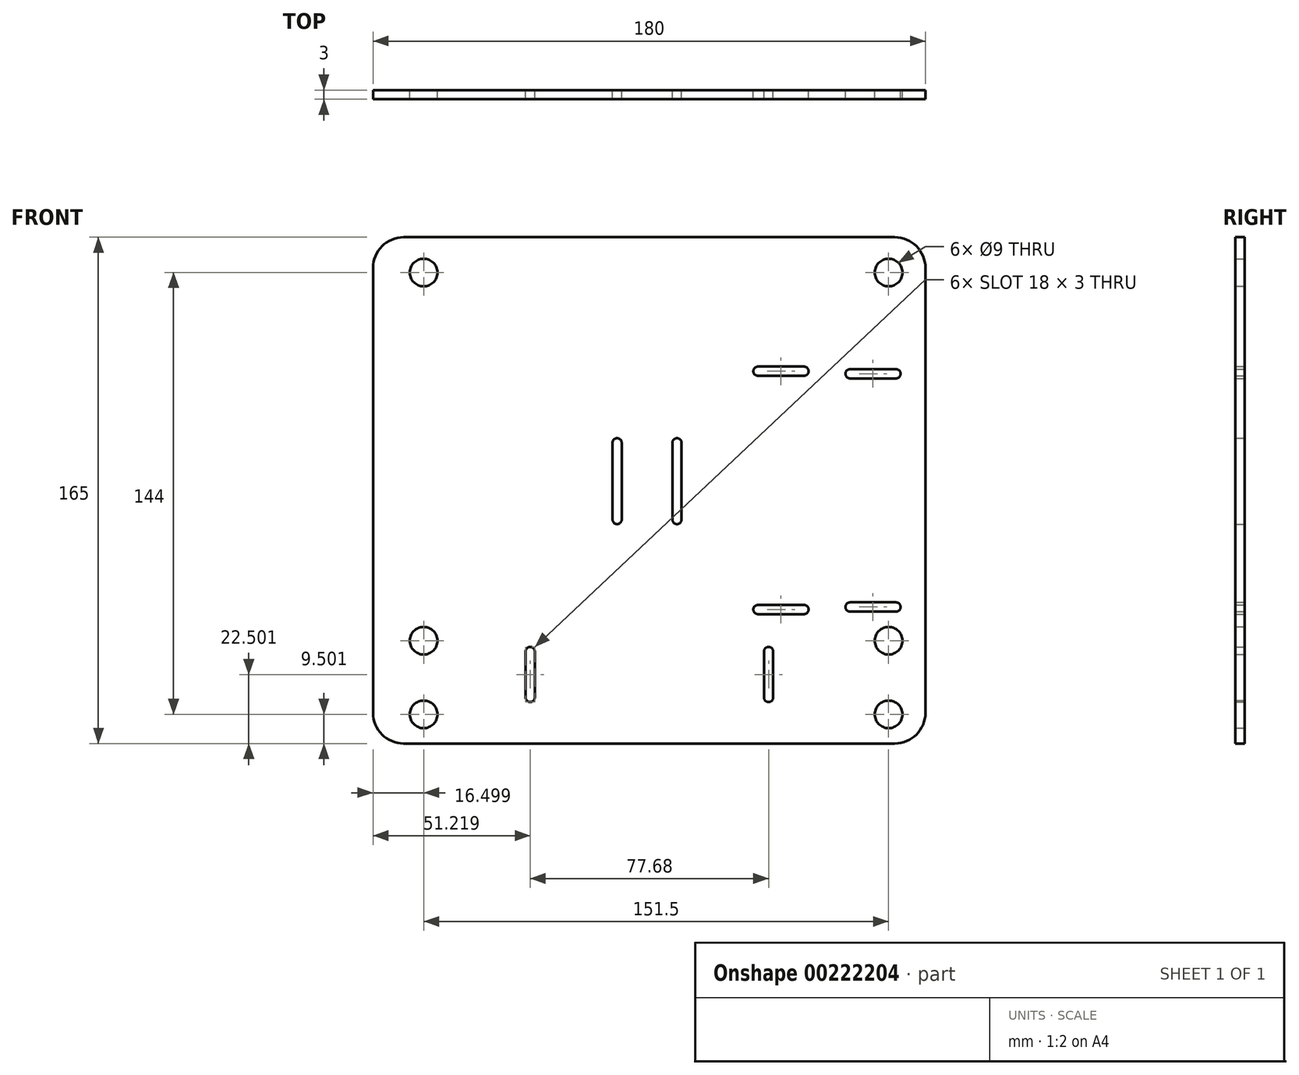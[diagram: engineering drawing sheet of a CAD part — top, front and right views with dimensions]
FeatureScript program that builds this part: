
annotation { "Feature Type Name" : "Feature", "Feature Type Description" : "" }
export const myFeature = defineFeature(function(context is Context, id is Id, definition is map)
    precondition{}
    {
        {
            var Q0;
            Q0=qCreatedBy(makeId("Front.planeOp"),FACE);
            var sketch = newSketch(context, id + "F0", { "sketchPlane" : qUnion([Q0])});
            skLineSegment(sketch, "E0", {"start": v(-133.42, 78.54) * mm, "end": v(-133.42, -66.46) * mm});
            skLineSegment(sketch, "E1", {"start": v(-123.42, -76.46) * mm, "end": v(36.58, -76.46) * mm});
            skLineSegment(sketch, "E2", {"start": v(46.58, -66.46) * mm, "end": v(46.58, 78.54) * mm});
            skLineSegment(sketch, "E3", {"start": v(36.58, 88.54) * mm, "end": v(-123.42, 88.54) * mm});
            skCircle(sketch, "E4", {"center": v(-116.92, -42.96) * mm, "radius": 4.5 * mm});
            skCircle(sketch, "E5", {"center": v(-116.92, -66.96) * mm, "radius": 4.5 * mm});
            skCircle(sketch, "E6", {"center": v(-116.92, 77.04) * mm, "radius": 4.5 * mm});
            skCircle(sketch, "E7.MirrorC", {"center": v(34.58, -66.96) * mm, "radius": 4.5 * mm});
            skCircle(sketch, "E8.MirrorC", {"center": v(34.58, -42.96) * mm, "radius": 4.5 * mm});
            skCircle(sketch, "E9.MirrorC", {"center": v(34.58, 77.04) * mm, "radius": 4.5 * mm});
            skLineSegment(sketch, "E10", {"start": v(-55.39, -3.46) * mm, "end": v(-55.39, 21.54) * mm});
            skLineSegment(sketch, "E11", {"start": v(-52.39, -3.46) * mm, "end": v(-52.39, 21.54) * mm});
            skArc(sketch, "E12", {"start": v(-52.39, 21.54) * mm, "mid": v(-53.89, 23.04) * mm, "end": v(-55.39, 21.54) * mm});
            skPoint(sketch, "E13.endSnap0", {"position": v(-52.39, 9.04) * mm});
            skArc(sketch, "E14.MirrorCS", {"start": v(-52.37, -3.46) * mm, "mid": v(-53.87, -4.96) * mm, "end": v(-55.37, -3.46) * mm});
            skLineSegment(sketch, "E15.MirrorCS", {"start": v(-55.39, 12.58) * mm, "end": v(-55.39, -3.46) * mm});
            skLineSegment(sketch, "E16", {"start": v(-35.87, -3.46) * mm, "end": v(-35.87, 21.54) * mm});
            skLineSegment(sketch, "E17", {"start": v(-32.87, -3.46) * mm, "end": v(-32.87, 21.54) * mm});
            skArc(sketch, "E18", {"start": v(-32.87, 21.54) * mm, "mid": v(-34.37, 23.04) * mm, "end": v(-35.87, 21.54) * mm});
            skPoint(sketch, "E19.endSnap0", {"position": v(-32.87, 9.04) * mm});
            skArc(sketch, "E20.MirrorCS", {"start": v(-32.87, -3.46) * mm, "mid": v(-34.37, -4.96) * mm, "end": v(-35.87, -3.46) * mm});
            skLineSegment(sketch, "E21.MirrorCS", {"start": v(-35.89, 20.16) * mm, "end": v(-35.89, -4.84) * mm});
            skLineSegment(sketch, "E22", {"start": v(-6.02, -62.84) * mm, "end": v(-6.02, -46.46) * mm});
            skLineSegment(sketch, "E23", {"start": v(-3.02, -61.46) * mm, "end": v(-3.02, -46.46) * mm});
            skArc(sketch, "E24", {"start": v(-3.02, -46.46) * mm, "mid": v(-4.52, -44.96) * mm, "end": v(-6.02, -46.46) * mm});
            skArc(sketch, "E25.MirrorCS", {"start": v(-3.02, -61.46) * mm, "mid": v(-4.52, -62.96) * mm, "end": v(-6.02, -61.46) * mm});
            skLineSegment(sketch, "E26.MirrorCS", {"start": v(-6.02, -46.46) * mm, "end": v(-6.02, -62.84) * mm});
            skLineSegment(sketch, "E27.MirrorCS", {"start": v(-80.7, -61.46) * mm, "end": v(-80.7, -46.46) * mm});
            skArc(sketch, "E28.MirrorCS", {"start": v(-83.7, -46.46) * mm, "mid": v(-82.2, -44.96) * mm, "end": v(-80.7, -46.46) * mm});
            skLineSegment(sketch, "E29.MirrorCS", {"start": v(-83.7, -61.46) * mm, "end": v(-83.7, -46.46) * mm});
            skLineSegment(sketch, "E30.MirrorCS", {"start": v(-80.7, -46.46) * mm, "end": v(-80.7, -61.46) * mm});
            skArc(sketch, "E31.MirrorCS", {"start": v(-83.7, -61.46) * mm, "mid": v(-82.2, -62.96) * mm, "end": v(-80.7, -61.46) * mm});
            skLineSegment(sketch, "E32", {"start": v(21.9, -30.46) * mm, "end": v(37, -30.46) * mm});
            skLineSegment(sketch, "E33", {"start": v(22, -33.46) * mm, "end": v(37, -33.46) * mm});
            skArc(sketch, "E34", {"start": v(37, -33.46) * mm, "mid": v(38.5, -31.96) * mm, "end": v(37, -30.46) * mm});
            skArc(sketch, "E35.MirrorCS", {"start": v(22, -33.46) * mm, "mid": v(20.5, -31.96) * mm, "end": v(22, -30.46) * mm});
            skLineSegment(sketch, "E36.MirrorCS", {"start": v(37, -30.46) * mm, "end": v(21.9, -30.46) * mm});
            skArc(sketch, "E37.MirrorCS", {"start": v(37, 45.54) * mm, "mid": v(38.5, 44.04) * mm, "end": v(37, 42.54) * mm});
            skLineSegment(sketch, "E38.MirrorCS", {"start": v(22, 45.54) * mm, "end": v(37, 45.54) * mm});
            skLineSegment(sketch, "E39.MirrorCS", {"start": v(37, 42.54) * mm, "end": v(22, 42.54) * mm});
            skArc(sketch, "E40.MirrorCS", {"start": v(22, 45.54) * mm, "mid": v(20.5, 44.04) * mm, "end": v(22, 42.54) * mm});
            skLineSegment(sketch, "E41", {"start": v(-8, -31.3) * mm, "end": v(7, -31.3) * mm});
            skLineSegment(sketch, "E42", {"start": v(0, -34.3) * mm, "end": v(7, -34.3) * mm});
            skArc(sketch, "E43", {"start": v(7, -34.3) * mm, "mid": v(8.5, -32.8) * mm, "end": v(7, -31.3) * mm});
            skLineSegment(sketch, "E44.MirrorCS", {"start": v(7, -31.3) * mm, "end": v(-8, -31.3) * mm});
            skLineSegment(sketch, "E45.MirrorCS", {"start": v(-8, 43.38) * mm, "end": v(7, 43.38) * mm});
            skArc(sketch, "E46.MirrorCS", {"start": v(7, 46.38) * mm, "mid": v(8.5, 44.88) * mm, "end": v(7, 43.38) * mm});
            skLineSegment(sketch, "E47.MirrorCS", {"start": v(-8, 46.38) * mm, "end": v(7, 46.38) * mm});
            skLineSegment(sketch, "E48.MirrorCS", {"start": v(7, 43.38) * mm, "end": v(-8, 43.38) * mm});
            skArc(sketch, "E49.MirrorCS", {"start": v(-8, 46.38) * mm, "mid": v(-9.5, 44.88) * mm, "end": v(-8, 43.38) * mm});
            skLineSegment(sketch, "E50", {"start": v(7, -34.3) * mm, "end": v(-8, -34.3) * mm});
            skArc(sketch, "E51", {"start": v(-8, -31.3) * mm, "mid": v(-9.5, -32.8) * mm, "end": v(-8, -34.3) * mm});
            skPoint(sketch, "E52.MirrorCS.center.orphan", {"position": v(0, -32.8) * mm});
            skPoint(sketch, "E53.visualSharp", {"position": v(-133.42, 88.54) * mm});
            skArc(sketch, "E53.filletArc", {"start": v(-123.42, 88.54) * mm, "mid": v(-130.5, 85.61) * mm, "end": v(-133.42, 78.54) * mm});
            skPoint(sketch, "E54.visualSharp", {"position": v(-133.42, -76.46) * mm});
            skArc(sketch, "E54.filletArc", {"start": v(-133.42, -66.46) * mm, "mid": v(-130.5, -73.53) * mm, "end": v(-123.42, -76.46) * mm});
            skPoint(sketch, "E55.visualSharp", {"position": v(46.58, -76.46) * mm});
            skArc(sketch, "E55.filletArc", {"start": v(36.58, -76.46) * mm, "mid": v(43.65, -73.53) * mm, "end": v(46.58, -66.46) * mm});
            skPoint(sketch, "E56.visualSharp", {"position": v(46.58, 88.54) * mm});
            skArc(sketch, "E56.filletArc", {"start": v(46.58, 78.54) * mm, "mid": v(43.65, 85.61) * mm, "end": v(36.58, 88.54) * mm});
            skLineSegment(sketch, "E57", {"start": v(-52.39, 21.54) * mm, "end": v(-52.37, -3.46) * mm});
            skLineSegment(sketch, "E58", {"start": v(-55.39, 21.54) * mm, "end": v(-55.37, -3.46) * mm});
            skSolve(sketch);
        }
        {
            var Q0;
            Q0=makeQuery(id+"F0.imprint","IMPRINT",FACE,{"disambiguationData":[TD([[makeQuery(id+"F0.imprint","IMPRINT",EDGE,{"derivedFrom":sQuery(id+"F0.wireOp",EDGE,"E0")}),1.0]])]});
            extrude(context, id + "F1", {"entities" : qUnion([Q0]), "depth" : 3 * mm, "offsetDistance" : 25 * mm});
        }
    });
